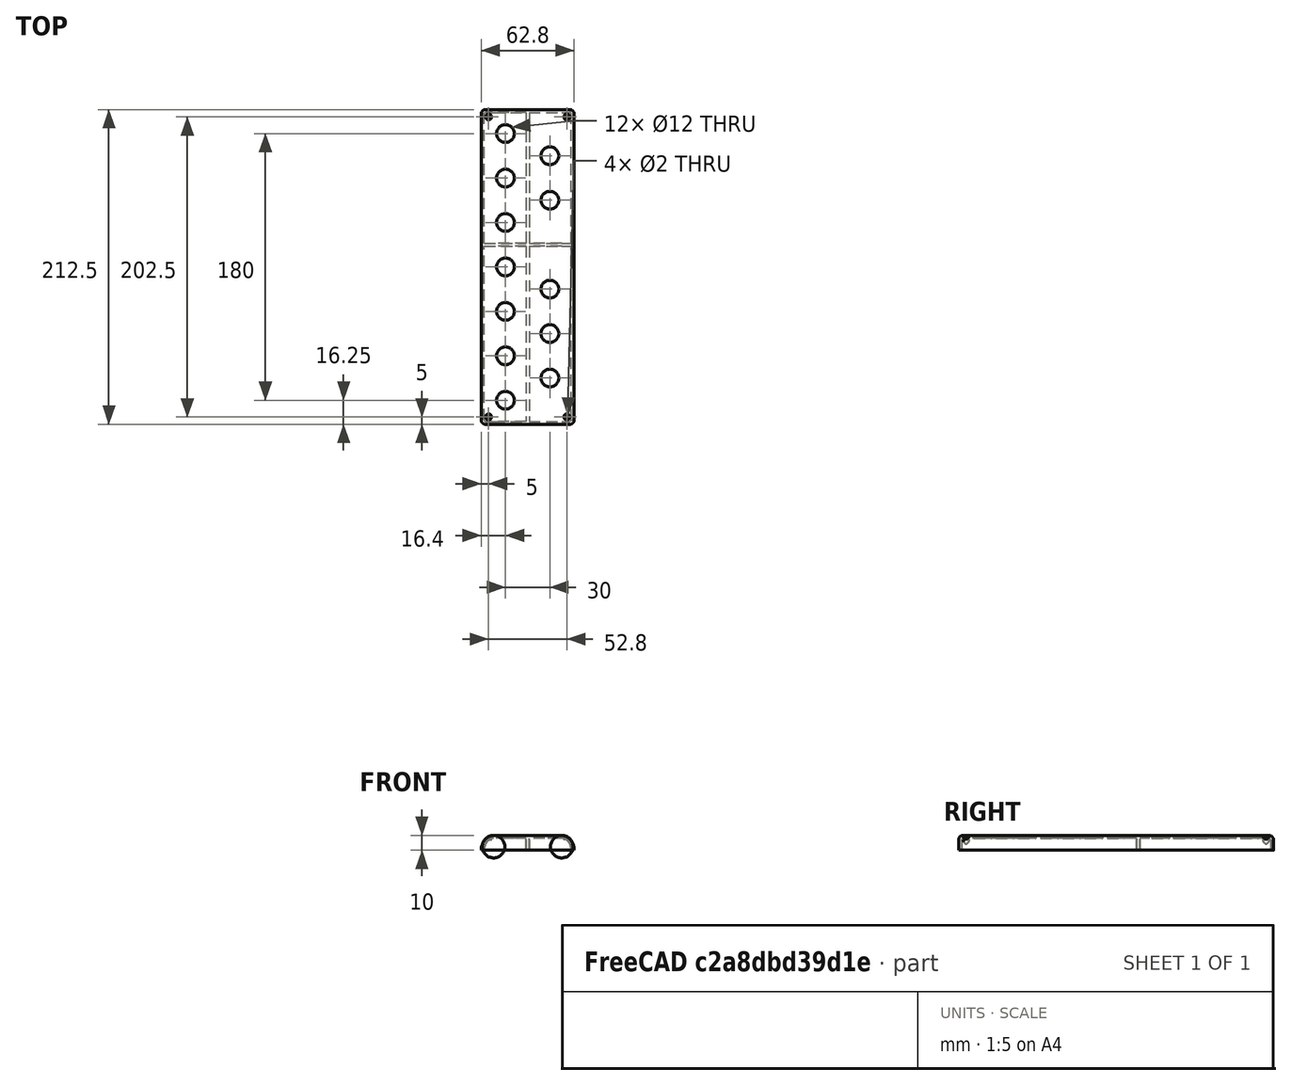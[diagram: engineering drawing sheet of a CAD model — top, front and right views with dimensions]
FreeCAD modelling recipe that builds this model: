
FCSTD DOCUMENT  (FreeCAD 0.20R28671 (Git))
Label: cubierta
License: All rights reserved
LicenseURL: http://en.wikipedia.org/wiki/All_rights_reserved
objects: TechDraw::DrawViewDimension×25, Sketcher::SketchObject×8, TechDraw::DrawViewAnnotation×5, PartDesign::Pad×4, PartDesign::Pocket×2, PartDesign::Plane×2, TechDraw::DrawProjGroupItem×2, TechDraw::DrawViewSection×2, PartDesign::Fillet×1, PartDesign::Thickness×1, PartDesign::Body×1, TechDraw::DrawSVGTemplate×1, TechDraw::DrawProjGroup×1, TechDraw::DrawPage×1
note: 27 computed .brp shape members not serialized (recipe doc carries the construction recipe); baked Part::Feature solids carry a one-line shape summary decoded from their .brp

FEATURE [Sketcher::SketchObject] Sketch
  FullyConstrained = true
  MapMode = 5
  Placement = pos=(0,0,0) rot=(1,0,0;1.5708rad)
  Support = -> [XZ_Plane]
  sketch-geometry (12):
    g0: LineSegment StartX=0 StartY=1.2153e-11 StartZ=0 EndX=-31.4 EndY=5.028e-13 EndZ=0
    g1: LineSegment StartX=0 StartY=1.2153e-11 StartZ=0 EndX=31.4 EndY=1.2153e-11 EndZ=0
    g2: LineSegment StartX=-23 StartY=10 StartZ=0 EndX=0 EndY=10 EndZ=0
    g3: LineSegment StartX=0 StartY=10 StartZ=0 EndX=23 EndY=10 EndZ=0
    g4: LineSegment StartX=-31.4 StartY=5.028e-13 StartZ=0 EndX=-28 EndY=0 EndZ=0
    g5: LineSegment StartX=-28 StartY=0 StartZ=0 EndX=-28 EndY=7 EndZ=0
    g6: ArcOfCircle CenterX=-23 CenterY=2.41173 CenterZ=0 NormalX=0 NormalY=0 NormalZ=1 AngleXU=0 Radius=7.58827 StartAngle=1.5708 EndAngle=2.49226
    g7: ArcOfCircle CenterX=-19.8231 CenterY=-1.6781e-06 CenterZ=0 NormalX=0 NormalY=0 NormalZ=1 AngleXU=0 Radius=11.5769 StartAngle=2.49226 EndAngle=3.14159
    g8: LineSegment StartX=-31.4 StartY=5.028e-13 StartZ=0 EndX=-31.4 EndY=7 EndZ=0
    g9: ArcOfCircle CenterX=23 CenterY=2.41173 CenterZ=0 NormalX=0 NormalY=0 NormalZ=1 AngleXU=0 Radius=7.58827 StartAngle=0.649332 EndAngle=1.5708
    g10: ArcOfCircle CenterX=19.8231 CenterY=7.13302e-06 CenterZ=0 NormalX=0 NormalY=0 NormalZ=1 AngleXU=0 Radius=11.5769 StartAngle=6.28318 EndAngle=6.93252
    g11: LineSegment StartX=31.4 StartY=1.2153e-11 StartZ=0 EndX=31.4 EndY=10 EndZ=0
  constraints (35):
    c: Coincident(g0,g-1)
    c: PointOnObject(g0,g-1)
    c: Coincident(g1,g0)
    c: Horizontal(g1)
    c: Equal(g1,g0)
    c: DistanceX(g0,g1) = 62.8
    c: Coincident(g3,g2)
    c: Horizontal(g3)
    c: Vertical(g0,g2)
    c: Equal(g2,g3)
    c: DistanceX(g2,g3) = 46
    c: DistanceY(g0,g2) = 10
    c: Horizontal(g2)
    c: Coincident(g4,g0)
    c: PointOnObject(g4,g0)
    c: Coincident(g5,g4)
    c: Vertical(g5)
    c: DistanceX(g0,g4) = 3.4
    c: DistanceY(g5,g5) = 7
    c: Tangent(g6,g2) = 1.5708
    c: Coincident(g7,g0)
    c: Horizontal(g6,g5)
    c: Tangent(g7,g6) = -1.5708
    c: Coincident(g8,g0)
    c: Vertical(g8)
    c: Tangent(g7,g8)
    c: Horizontal(g8,g5)
    c: Coincident(g10,g1)
    c: Tangent(g9,g3) = 1.5708
    c: Coincident(g11,g1)
    c: Vertical(g11)
    c: Horizontal(g11,g3)
    c: Tangent(g10,g11)
    c: Equal(g9,g6)
    c: Tangent(g9,g10) = -1.5708
FEATURE [PartDesign::Pad] Pad
  Direction = (0,-1,-2e-16)
  Length = 212.5
  Length2 = 100
  Placement = pos=(0,0,0) rot=(1,0,0;1.5708rad)
  Profile = -> Sketch
  ReferenceAxis = -> Sketch [N_Axis]
  Type = 0
FEATURE [PartDesign::Fillet] Fillet
  Base = -> Pad [Edge19,Edge18]
  BaseFeature = -> Pad
  Placement = pos=(0,0,0) rot=(1,0,0;1.5708rad)
  Radius = 3
  SupportTransform = false
  UseAllEdges = false
FEATURE [PartDesign::Thickness] Thickness
  Base = -> Fillet [Face7,Face1]
  BaseFeature = -> Fillet
  Intersection = false
  Join = 0
  Mode = 0
  Reversed = true
  SupportTransform = false
  Value = 2
FEATURE [Sketcher::SketchObject] Sketch001
  ExternalGeometry = -> [Thickness]
  FullyConstrained = true
  MapMode = 5
  Placement = pos=(0,0,1.2153e-11) rot=(1,0,0;3.14159rad)
  Support = -> [Thickness]
  sketch-geometry (12):
    g0: LineSegment StartX=-31.4 StartY=207.5 StartZ=0 EndX=-26.4 EndY=207.5 EndZ=0
    g1: LineSegment StartX=-26.4 StartY=207.5 StartZ=0 EndX=-26.4 EndY=212.5 EndZ=0
    g2: LineSegment StartX=26.4 StartY=212.5 StartZ=0 EndX=26.4 EndY=207.5 EndZ=0
    g3: LineSegment StartX=26.4 StartY=207.5 StartZ=0 EndX=31.4 EndY=207.5 EndZ=0
    g4: LineSegment StartX=-31.4 StartY=5 StartZ=0 EndX=-26.4 EndY=5 EndZ=0
    g5: LineSegment StartX=-26.4 StartY=5 StartZ=0 EndX=-26.4 EndY=0 EndZ=0
    g6: LineSegment StartX=26.4 StartY=0 StartZ=0 EndX=26.4 EndY=5 EndZ=0
    g7: LineSegment StartX=26.4 StartY=5 StartZ=0 EndX=31.4 EndY=5 EndZ=0
    g8: Circle CenterX=-26.4 CenterY=207.5 CenterZ=0 NormalX=0 NormalY=0 NormalZ=1 AngleXU=0 Radius=2
    g9: Circle CenterX=26.4 CenterY=207.5 CenterZ=0 NormalX=0 NormalY=0 NormalZ=1 AngleXU=0 Radius=2
    g10: Circle CenterX=-26.4 CenterY=5 CenterZ=0 NormalX=0 NormalY=0 NormalZ=1 AngleXU=0 Radius=2
    g11: Circle CenterX=26.4 CenterY=5 CenterZ=0 NormalX=0 NormalY=0 NormalZ=1 AngleXU=0 Radius=2
  constraints (36):
    c: PointOnObject(g1,g-7)
    c: PointOnObject(g0,g-5)
    c: PointOnObject(g2,g-8)
    c: PointOnObject(g3,g-6)
    c: PointOnObject(g7,g-6)
    c: PointOnObject(g6,g-4)
    c: PointOnObject(g5,g-3)
    c: PointOnObject(g4,g-5)
    c: Vertical(g5)
    c: Horizontal(g4)
    c: Vertical(g6)
    c: Horizontal(g7)
    c: Vertical(g1)
    c: Horizontal(g0)
    c: Horizontal(g3)
    c: Vertical(g2)
    c: Coincident(g9,g2)
    c: Coincident(g9,g3)
    c: Coincident(g1,g8)
    c: Coincident(g0,g8)
    c: Coincident(g10,g4)
    c: Coincident(g10,g5)
    c: Coincident(g11,g6)
    c: Coincident(g11,g7)
    c: Equal(g7,g6)
    c: Equal(g6,g5)
    c: Equal(g5,g4)
    c: Equal(g4,g3)
    c: Equal(g3,g2)
    c: Equal(g2,g1)
    c: Equal(g1,g0)
    c: DistanceY(g1,g1) = 5
    c: Equal(g8,g9)
    c: Equal(g9,g11)
    c: Equal(g11,g10)
    c: Diameter(g10) = 4
FEATURE [PartDesign::Pocket] Pocket
  BaseFeature = -> Thickness
  Direction = (0,0,1)
  Length = 5
  Length2 = 100
  Profile = -> Sketch001
  Type = 1
FEATURE [PartDesign::Plane] DatumPlane
  AttachmentOffset = pos=(0,0,-7) rot=(0,0,1;0rad)
  Length = 119.841
  MapMode = 5
  Placement = pos=(-2.5971e-12,0,7) rot=(1,0,0;3.14159rad)
  ResizeMode = 0
  Support = -> [Pocket]
  Width = 282.746
FEATURE [Sketcher::SketchObject] Sketch002
  ExternalGeometry = -> [Pocket]
  FullyConstrained = true
  MapMode = 5
  Placement = pos=(-2.5971e-12,0,7) rot=(1,0,0;3.14159rad)
  Support = -> [DatumPlane]
  sketch-geometry (8):
    g0: Circle CenterX=26.4 CenterY=5 CenterZ=0 NormalX=0 NormalY=0 NormalZ=1 AngleXU=0 Radius=2
    g1: Circle CenterX=-26.4 CenterY=5 CenterZ=0 NormalX=0 NormalY=0 NormalZ=1 AngleXU=0 Radius=2
    g2: Circle CenterX=-26.4 CenterY=207.5 CenterZ=0 NormalX=0 NormalY=0 NormalZ=1 AngleXU=0 Radius=2
    g3: Circle CenterX=26.4 CenterY=207.5 CenterZ=0 NormalX=0 NormalY=0 NormalZ=1 AngleXU=0 Radius=2
    g4: Circle CenterX=-26.4 CenterY=207.5 CenterZ=0 NormalX=0 NormalY=0 NormalZ=1 AngleXU=0 Radius=1
    g5: Circle CenterX=26.4 CenterY=207.5 CenterZ=0 NormalX=0 NormalY=0 NormalZ=1 AngleXU=0 Radius=1
    g6: Circle CenterX=26.4 CenterY=5 CenterZ=0 NormalX=0 NormalY=0 NormalZ=1 AngleXU=0 Radius=1
    g7: Circle CenterX=-26.4 CenterY=5 CenterZ=0 NormalX=0 NormalY=0 NormalZ=1 AngleXU=0 Radius=1
  constraints (20):
    c: PointOnObject(g-10,g0)
    c: PointOnObject(g-10,g0)
    c: PointOnObject(g-9,g0)
    c: PointOnObject(g-7,g1)
    c: PointOnObject(g-8,g1)
    c: PointOnObject(g-8,g1)
    c: PointOnObject(g-4,g2)
    c: PointOnObject(g-4,g2)
    c: PointOnObject(g-3,g2)
    c: PointOnObject(g-5,g3)
    c: PointOnObject(g-6,g3)
    c: PointOnObject(g-5,g3)
    c: Coincident(g4,g2)
    c: Coincident(g5,g3)
    c: Coincident(g6,g0)
    c: Coincident(g7,g1)
    c: Equal(g7,g6)
    c: Equal(g6,g5)
    c: Equal(g5,g4)
    c: Diameter(g4) = 2
FEATURE [PartDesign::Pad] Pad001
  BaseFeature = -> Pocket
  Direction = (3.71e-13,0,-1)
  Length = 0.9
  Length2 = 100
  Profile = -> Sketch002
  ReferenceAxis = -> Sketch002 [N_Axis]
  Reversed = true
  Type = 0
FEATURE [Sketcher::SketchObject] Sketch003
  ExternalGeometry = -> [Pad001]
  FullyConstrained = true
  MapMode = 5
  Placement = pos=(-2.5971e-12,0,7) rot=(1,0,0;3.14159rad)
  Support = -> [Pad001]
  sketch-geometry (33):
    g0: Circle CenterX=-15 CenterY=16.25 CenterZ=0 NormalX=0 NormalY=0 NormalZ=1 AngleXU=0 Radius=6
    g1: Circle CenterX=-15 CenterY=46.25 CenterZ=0 NormalX=0 NormalY=0 NormalZ=1 AngleXU=0 Radius=6
    g2: Circle CenterX=-15 CenterY=76.25 CenterZ=0 NormalX=0 NormalY=0 NormalZ=1 AngleXU=0 Radius=6
    g3: Circle CenterX=-15 CenterY=106.25 CenterZ=0 NormalX=0 NormalY=0 NormalZ=1 AngleXU=0 Radius=6
    g4: Circle CenterX=-15 CenterY=136.25 CenterZ=0 NormalX=0 NormalY=0 NormalZ=1 AngleXU=0 Radius=6
    g5: LineSegment StartX=-15 StartY=46.25 StartZ=0 EndX=-15 EndY=16.25 EndZ=0
    g6: LineSegment StartX=-15 StartY=16.25 StartZ=0 EndX=-15 EndY=46.25 EndZ=0
    g7: LineSegment StartX=-15 StartY=46.25 StartZ=0 EndX=-15 EndY=76.25 EndZ=0
    g8: LineSegment StartX=-15 StartY=76.25 StartZ=0 EndX=-15 EndY=106.25 EndZ=0
    g9: LineSegment StartX=-15 StartY=106.25 StartZ=0 EndX=-15 EndY=136.25 EndZ=0
    g10: LineSegment StartX=-15 StartY=136.25 StartZ=0 EndX=-15 EndY=106.25 EndZ=0
    g11: Circle CenterX=15 CenterY=31.25 CenterZ=0 NormalX=0 NormalY=0 NormalZ=1 AngleXU=0 Radius=6
    g12: Circle CenterX=15 CenterY=61.25 CenterZ=0 NormalX=0 NormalY=0 NormalZ=1 AngleXU=0 Radius=6
    g13: Circle CenterX=15 CenterY=121.25 CenterZ=0 NormalX=0 NormalY=0 NormalZ=1 AngleXU=0 Radius=6
    g14: Circle CenterX=15 CenterY=151.25 CenterZ=0 NormalX=0 NormalY=0 NormalZ=1 AngleXU=0 Radius=6
    g15: LineSegment StartX=15 StartY=31.25 StartZ=0 EndX=15 EndY=61.25 EndZ=0
    g16: LineSegment StartX=15 StartY=91.25 StartZ=0 EndX=15 EndY=121.25 EndZ=0
    g17: LineSegment StartX=15 StartY=121.25 StartZ=0 EndX=15 EndY=151.25 EndZ=0
    g18: LineSegment StartX=15 StartY=31.25 StartZ=0 EndX=-15 EndY=46.25 EndZ=0
    g19: LineSegment StartX=15 StartY=31.25 StartZ=0 EndX=-15 EndY=16.25 EndZ=0
    g20: LineSegment StartX=15 StartY=91.25 StartZ=0 EndX=-15 EndY=76.25 EndZ=0
    g21: LineSegment StartX=15 StartY=91.25 StartZ=0 EndX=-15 EndY=106.25 EndZ=0
    g22: LineSegment StartX=15 StartY=31.25 StartZ=0 EndX=0 EndY=31.25 EndZ=0
    g23: LineSegment StartX=0 StartY=31.25 StartZ=0 EndX=-15 EndY=31.25 EndZ=0
    g24: LineSegment StartX=0 StartY=0 StartZ=0 EndX=0 EndY=212.5 EndZ=0
    g25: LineSegment StartX=-15 StartY=16.25 StartZ=0 EndX=-15 EndY=0 EndZ=0
    g26: Circle CenterX=15 CenterY=181.25 CenterZ=0 NormalX=0 NormalY=0 NormalZ=1 AngleXU=0 Radius=6
    g27: Circle CenterX=-15 CenterY=166.25 CenterZ=0 NormalX=0 NormalY=0 NormalZ=1 AngleXU=0 Radius=6
    g28: Circle CenterX=-15 CenterY=196.25 CenterZ=0 NormalX=0 NormalY=0 NormalZ=1 AngleXU=0 Radius=6
    g29: LineSegment StartX=15 StartY=181.25 StartZ=0 EndX=15 EndY=151.25 EndZ=0
    g30: LineSegment StartX=-15 StartY=136.25 StartZ=0 EndX=-15 EndY=166.25 EndZ=0
    g31: LineSegment StartX=-15 StartY=166.25 StartZ=0 EndX=-15 EndY=196.25 EndZ=0
    g32: LineSegment StartX=-15 StartY=196.25 StartZ=0 EndX=-15 EndY=212.5 EndZ=0
  constraints (85):
    c: Equal(g0,g1)
    c: Equal(g1,g2)
    c: Equal(g2,g3)
    c: Equal(g3,g4)
    c: Coincident(g5,g0)
    c: Vertical(g5)
    c: Coincident(g6,g0)
    c: Coincident(g6,g1)
    c: Vertical(g6)
    c: Coincident(g7,g1)
    c: Coincident(g7,g2)
    c: Coincident(g8,g2)
    c: Coincident(g8,g3)
    c: Coincident(g9,g3)
    c: Coincident(g9,g4)
    c: Coincident(g10,g4)
    c: Equal(g8,g7)
    c: Equal(g7,g6)
    c: Equal(g6,g5)
    c: Equal(g5,g9)
    c: Equal(g9,g10)
    c: Vertical(g8)
    c: Vertical(g7)
    c: Vertical(g9)
    c: Vertical(g10)
    c: Equal(g14,g13)
    c: Equal(g12,g11)
    c: Equal(g11,g0)
    c: Coincident(g15,g11)
    c: Coincident(g15,g12)
    c: Vertical(g15)
    c: Coincident(g16,g13)
    c: Coincident(g17,g13)
    c: Coincident(g17,g14)
    c: Vertical(g17)
    c: Vertical(g16)
    c: Equal(g17,g16)
    c: Equal(g16,g15)
    c: Equal(g15,g6)
    c: Coincident(g18,g11)
    c: Coincident(g19,g11)
    c: Coincident(g19,g0)
    c: Equal(g19,g18)
    c: Coincident(g20,g2)
    c: Coincident(g21,g3)
    c: Equal(g21,g20)
    c: Coincident(g22,g11)
    c: Horizontal(g22)
    c: Coincident(g23,g22)
    c: PointOnObject(g23,g5)
    c: Horizontal(g23)
    c: Equal(g23,g22)
    c: Coincident(g24,g-1)
    c: Coincident(g24,g-3)
    c: PointOnObject(g22,g24)
    c: Coincident(g25,g0)
    c: PointOnObject(g25,g-1)
    c: Vertical(g25)
    c: Equal(g26,g27)
    c: Equal(g27,g28)
    c: Equal(g28,g4)
    c: Coincident(g29,g26)
    c: Coincident(g29,g14)
    c: Coincident(g30,g4)
    c: Coincident(g30,g27)
    c: Coincident(g31,g27)
    c: Coincident(g31,g28)
    c: Vertical(g31)
    c: Vertical(g30)
    c: Vertical(g29)
    c: Equal(g31,g30)
    c: Equal(g30,g29)
    c: Equal(g29,g17)
    c: Coincident(g20,g16)
    c: Coincident(g16,g21)
    c: Coincident(g32,g28)
    c: Horizontal(g32,g24)
    c: Vertical(g32)
    c: Equal(g25,g32)
    c: Vertical(g16,g12)
    c: Equal(g14,g26)
    c: Diameter(g0) = 12
    c: DistanceX(g23,g11) = 30
    c: DistanceY(g0,g1) = 30
    c: Coincident(g18,g1)
FEATURE [PartDesign::Pocket] Pocket001
  BaseFeature = -> Pad001
  Direction = (-3.71e-13,0,1)
  Length = 5
  Length2 = 100
  Profile = -> Sketch003
  Type = 1
FEATURE [Sketcher::SketchObject] Sketch004
  ExternalGeometry = -> [Pocket001]
  FullyConstrained = true
  MapMode = 5
  Placement = pos=(0,0,1.2153e-11) rot=(1,0,0;3.14159rad)
  Support = -> [Pocket001]
  sketch-geometry (9):
    g0: LineSegment StartX=0 StartY=1 StartZ=0 EndX=-1 EndY=1 EndZ=0
    g1: LineSegment StartX=0 StartY=1 StartZ=0 EndX=1 EndY=1 EndZ=0
    g2: LineSegment StartX=-1 StartY=1 StartZ=0 EndX=-1 EndY=211.5 EndZ=0
    g3: LineSegment StartX=1 StartY=1 StartZ=0 EndX=1 EndY=211.5 EndZ=0
    g4: LineSegment StartX=-1 StartY=211.5 StartZ=0 EndX=1 EndY=211.5 EndZ=0
    g5: LineSegment StartX=0 StartY=2 StartZ=0 EndX=0 EndY=1 EndZ=0
    g6: LineSegment StartX=0 StartY=1 StartZ=0 EndX=0 EndY=0 EndZ=0
    g7: LineSegment StartX=0 StartY=210.5 StartZ=0 EndX=0 EndY=211.5 EndZ=0
    g8: LineSegment StartX=0 StartY=211.5 StartZ=0 EndX=0 EndY=212.5 EndZ=0
  constraints (24):
    c: Coincident(g2,g0)
    c: Vertical(g2)
    c: Coincident(g3,g1)
    c: Vertical(g3)
    c: Coincident(g4,g2)
    c: Coincident(g4,g3)
    c: Horizontal(g4)
    c: Equal(g0,g1)
    c: DistanceX(g0,g1) = 2
    c: Coincident(g0,g1)
    c: Horizontal(g0)
    c: Coincident(g5,g-4)
    c: Coincident(g5,g0)
    c: Vertical(g5)
    c: Coincident(g6,g0)
    c: Coincident(g6,g-1)
    c: Equal(g6,g5)
    c: Horizontal(g1)
    c: Coincident(g7,g-5)
    c: PointOnObject(g7,g4)
    c: Coincident(g8,g7)
    c: Coincident(g8,g-3)
    c: Vertical(g8)
    c: Equal(g8,g7)
FEATURE [PartDesign::Pad] Pad002
  BaseFeature = -> Pocket001
  Direction = (3.71e-13,0,-1)
  Length = 10
  Length2 = 100
  Profile = -> Sketch004
  ReferenceAxis = -> Sketch004 [N_Axis]
  Type = 3
  UpToFace = -> Pocket001 [Face64]
FEATURE [Sketcher::SketchObject] Sketch005
  ExternalGeometry = -> [Pad002]
  FullyConstrained = true
  MapMode = 5
  Placement = pos=(0,0,1.2153e-11) rot=(1,0,0;3.14159rad)
  Support = -> [Pad002]
  sketch-geometry (6):
    g0: LineSegment StartX=-31.4 StartY=92.25 StartZ=0 EndX=31.4 EndY=92.25 EndZ=0
    g1: LineSegment StartX=31.4 StartY=92.25 StartZ=0 EndX=31.4 EndY=90.25 EndZ=0
    g2: LineSegment StartX=31.4 StartY=90.25 StartZ=0 EndX=-31.4 EndY=90.25 EndZ=0
    g3: LineSegment StartX=-31.4 StartY=90.25 StartZ=0 EndX=-31.4 EndY=92.25 EndZ=0
    g4: LineSegment StartX=-15 StartY=76.25 StartZ=0 EndX=-15 EndY=90.25 EndZ=0
    g5: LineSegment StartX=-15 StartY=106.25 StartZ=0 EndX=-15 EndY=92.25 EndZ=0
  constraints (18):
    c: Coincident(g0,g1)
    c: Coincident(g1,g2)
    c: Coincident(g2,g3)
    c: Coincident(g3,g0)
    c: Horizontal(g0)
    c: Horizontal(g2)
    c: Vertical(g1)
    c: Vertical(g3)
    c: DistanceY(g2,g0) = 2
    c: Coincident(g4,g-6)
    c: PointOnObject(g4,g2)
    c: Vertical(g4)
    c: Coincident(g5,g-5)
    c: PointOnObject(g5,g0)
    c: Vertical(g5)
    c: Equal(g5,g4)
    c: PointOnObject(g0,g-7)
    c: PointOnObject(g0,g-8)
FEATURE [PartDesign::Plane] DatumPlane001
  Length = 63.3962
  MapMode = 1
  Placement = pos=(31.4,-92.25,1.2153e-11) rot=(0.57735,-0.57735,0.57735;2.0944rad)
  ResizeMode = 0
  Support = -> [Sketch005]
  Width = 103.125
FEATURE [Sketcher::SketchObject] Sketch006
  ExternalGeometry = -> [Sketch]
  FullyConstrained = true
  MapMode = 5
  Placement = pos=(31.4,-92.25,1.2153e-11) rot=(0.57735,-0.57735,0.57735;2.0944rad)
  Support = -> [DatumPlane001]
  sketch-geometry (6):
    g0: LineSegment StartX=-1.16297e-11 StartY=62.8 StartZ=0 EndX=1.216e-12 EndY=6.5654e-12 EndZ=0
    g1: LineSegment StartX=10 StartY=54.4 StartZ=0 EndX=10 EndY=8.4 EndZ=0
    g2: ArcOfCircle CenterX=-1.67812e-06 CenterY=51.2231 CenterZ=0 NormalX=0 NormalY=0 NormalZ=1 AngleXU=0 Radius=11.5769 StartAngle=0.921466 EndAngle=1.5708
    g3: ArcOfCircle CenterX=2.41173 CenterY=54.4 CenterZ=0 NormalX=0 NormalY=0 NormalZ=1 AngleXU=0 Radius=7.58827 StartAngle=-6.235e-13 EndAngle=0.921466
    g4: ArcOfCircle CenterX=2.41173 CenterY=8.4 CenterZ=0 NormalX=0 NormalY=0 NormalZ=1 AngleXU=0 Radius=7.58827 StartAngle=5.36172 EndAngle=6.28319
    g5: ArcOfCircle CenterX=7.13304e-06 CenterY=11.5769 CenterZ=0 NormalX=0 NormalY=0 NormalZ=1 AngleXU=0 Radius=11.5769 StartAngle=4.71239 EndAngle=5.36172
  constraints (16):
    c: Coincident(g0,g-5)
    c: Coincident(g0,g-1)
    c: Coincident(g1,g-4)
    c: Coincident(g1,g-7)
    c: Coincident(g2,g0)
    c: Coincident(g2,g-5)
    c: Tangent(g2,g-5)
    c: Coincident(g3,g2)
    c: Coincident(g3,g1)
    c: Tangent(g3,g-4)
    c: Coincident(g4,g1)
    c: Coincident(g4,g-8)
    c: Tangent(g4,g-7)
    c: Coincident(g5,g4)
    c: Coincident(g5,g0)
    c: Tangent(g5,g-8)
FEATURE [PartDesign::Pad] Pad003
  BaseFeature = -> Pad002
  Direction = (0,-1,0)
  Length = 2
  Length2 = 100
  Profile = -> Sketch006
  ReferenceAxis = -> Sketch006 [N_Axis]
  Reversed = true
  Type = 0
FEATURE [Sketcher::SketchObject] Sketch007
  ExternalGeometry = -> [Pad003]
  FullyConstrained = false
  MapMode = 5
  Placement = pos=(0,0,1.2153e-11) rot=(1,0,0;3.14159rad)
  Support = -> [Pad003]
  sketch-geometry (6):
    g0: LineSegment StartX=-31.4 StartY=92.25 StartZ=0 EndX=-31.4 EndY=91.25 EndZ=0
    g1: LineSegment StartX=-31.4 StartY=91.25 StartZ=0 EndX=-31.4 EndY=90.25 EndZ=0
    g2: LineSegment StartX=-37.6108 StartY=91.25 StartZ=0 EndX=52.1178 EndY=91.25 EndZ=0
    g3: LineSegment StartX=52.1178 StartY=91.25 StartZ=0 EndX=52.1178 EndY=227.634 EndZ=0
    g4: LineSegment StartX=52.1178 StartY=227.634 StartZ=0 EndX=-37.6108 EndY=227.634 EndZ=0
    g5: LineSegment StartX=-37.6108 StartY=227.634 StartZ=0 EndX=-37.6108 EndY=91.25 EndZ=0
  constraints (14):
    c: Coincident(g0,g-3)
    c: Vertical(g0)
    c: Coincident(g1,g0)
    c: Coincident(g1,g-4)
    c: Equal(g0,g1)
    c: Coincident(g2,g3)
    c: Coincident(g3,g4)
    c: Coincident(g4,g5)
    c: Coincident(g5,g2)
    c: Horizontal(g2)
    c: Horizontal(g4)
    c: Vertical(g3)
    c: Vertical(g5)
    c: PointOnObject(g0,g2)
FEATURE [PartDesign::Body] Body
  Group = -> [Sketch,Pad,Fillet,Thickness,Sketch001,Pocket,DatumPlane,Sketch002,Pad001,Sketch003,Pocket001,Sketch004,Pad002,Sketch005,DatumPlane001,Sketch006,Pad003,Sketch007]
  Origin = -> Origin
  Tip = -> Pad003
FEATURE [TechDraw::DrawSVGTemplate] Template
  EditableTexts = AUTHOR_NAME=Daniel García García; DATE=15-04-2022; DN=15; DOCUMENT_TYPE=Plano de pieza; PN=23; REVISION=1; SCALE=1:1; SHEET=15/15; SIZE=A4; TITLELINE-1=Cubierta Superior
  Height = 210
  Orientation = 1
  Width = 297
FEATURE [TechDraw::DrawProjGroupItem] ProjItem  label="Front"
  CoarseView = false
  Direction = (-1,0,0)
  Focus = 100
  HardHidden = false
  IsoCount = 0
  IsoHidden = false
  IsoVisible = false
  LockPosition = true
  Perspective = false
  Rotation = 0
  RotationVector = (0,-1,0)
  ScaleType = 2
  SeamHidden = false
  SeamVisible = true
  SmoothHidden = false
  SmoothVisible = true
  Source = -> [Pad003]
  Type = 0
  X = 0
  XDirection = (0,-1,0)
  Y = 0
FEATURE [TechDraw::DrawProjGroupItem] ProjItem001  label="Top"
  CoarseView = false
  Direction = (0,0,1)
  Focus = 100
  HardHidden = false
  IsoCount = 0
  IsoHidden = false
  IsoVisible = false
  LockPosition = true
  Perspective = false
  Rotation = 0
  RotationVector = (1,0,0)
  ScaleType = 2
  SeamHidden = false
  SeamVisible = true
  SmoothHidden = false
  SmoothVisible = true
  Source = -> [Pad003]
  Type = 4
  X = 0
  XDirection = (0,-1,0)
  Y = -90.7058
FEATURE [TechDraw::DrawProjGroup] ProjGroup
  Anchor = -> ProjItem
  AutoDistribute = true
  LockPosition = true
  ProjectionType = 0
  Rotation = 0
  ScaleType = 0
  Source = -> [Pad003]
  Views = -> [ProjItem,ProjItem001]
  X = 152.056
  Y = 178.296
  spacingX = 15
  spacingY = 15
FEATURE [TechDraw::DrawViewDimension] Dimension
  AngleOverride = false
  Arbitrary = false
  ArbitraryTolerances = false
  EqualTolerance = true
  ExtensionAngle = 0
  FormatSpec = %.2w
  FormatSpecOverTolerance = %+.2w
  FormatSpecUnderTolerance = %+.2w
  Inverted = false
  LineAngle = 0
  LockPosition = false
  MeasureType = 1
  OverTolerance = 0
  References2D = -> [ProjItem]
  Rotation = 0
  ScaleType = 0
  TheoreticalExact = false
  Type = 1
  UnderTolerance = 0
  X = 2.1598
  Y = 15.6269
FEATURE [TechDraw::DrawViewDimension] Dimension001
  AngleOverride = false
  Arbitrary = false
  ArbitraryTolerances = false
  EqualTolerance = true
  ExtensionAngle = 0
  FormatSpec = ⌀%.2w
  FormatSpecOverTolerance = %+.2w
  FormatSpecUnderTolerance = %+.2w
  Inverted = false
  LineAngle = 0
  LockPosition = false
  MeasureType = 1
  OverTolerance = 0
  References2D = -> [ProjItem001]
  Rotation = 0
  ScaleType = 0
  TheoreticalExact = false
  Type = 5
  UnderTolerance = 0
  X = -93.626
  Y = 7.7505
FEATURE [TechDraw::DrawViewDimension] Dimension002
  AngleOverride = false
  Arbitrary = false
  ArbitraryTolerances = false
  EqualTolerance = true
  ExtensionAngle = 0
  FormatSpec = %.2w
  FormatSpecOverTolerance = %+.2w
  FormatSpecUnderTolerance = %+.2w
  Inverted = false
  LineAngle = 0
  LockPosition = false
  MeasureType = 1
  OverTolerance = 0
  References2D = -> [ProjItem]
  Rotation = 0
  ScaleType = 0
  TheoreticalExact = false
  Type = 1
  UnderTolerance = 0
  X = 0.67922
  Y = -5.55649
FEATURE [TechDraw::DrawViewDimension] Dimension003
  AngleOverride = false
  Arbitrary = false
  ArbitraryTolerances = false
  EqualTolerance = true
  ExtensionAngle = 0
  FormatSpec = %.2w
  FormatSpecOverTolerance = %+.2w
  FormatSpecUnderTolerance = %+.2w
  Inverted = false
  LineAngle = 0
  LockPosition = false
  MeasureType = 1
  OverTolerance = 0
  References2D = -> [ProjItem]
  Rotation = 0
  ScaleType = 0
  TheoreticalExact = false
  Type = 2
  UnderTolerance = 0
  X = -115.985
  Y = 2.73584
FEATURE [TechDraw::DrawViewDimension] Dimension004
  AngleOverride = false
  Arbitrary = false
  ArbitraryTolerances = false
  EqualTolerance = true
  ExtensionAngle = 0
  FormatSpec = R%.2w
  FormatSpecOverTolerance = %+.2w
  FormatSpecUnderTolerance = %+.2w
  Inverted = false
  LineAngle = 0
  LockPosition = false
  MeasureType = 1
  OverTolerance = 0
  References2D = -> [ProjItem]
  Rotation = 0
  ScaleType = 0
  TheoreticalExact = false
  Type = 4
  UnderTolerance = 0
  X = -116.741
  Y = 16.5088
FEATURE [TechDraw::DrawViewDimension] Dimension005
  AngleOverride = false
  Arbitrary = false
  ArbitraryTolerances = false
  EqualTolerance = true
  ExtensionAngle = 0
  FormatSpec = %.2w
  FormatSpecOverTolerance = %+.2w
  FormatSpecUnderTolerance = %+.2w
  Inverted = false
  LineAngle = 0
  LockPosition = false
  MeasureType = 1
  OverTolerance = 0
  References2D = -> [ProjItem001]
  Rotation = 0
  ScaleType = 0
  TheoreticalExact = false
  Type = 2
  UnderTolerance = 0
  X = -129.814
  Y = 2.22098
FEATURE [TechDraw::DrawViewDimension] Dimension006
  AngleOverride = false
  Arbitrary = false
  ArbitraryTolerances = false
  EqualTolerance = true
  ExtensionAngle = 0
  FormatSpec = %.2w
  FormatSpecOverTolerance = %+.2w
  FormatSpecUnderTolerance = %+.2w
  Inverted = false
  LineAngle = 0
  LockPosition = false
  MeasureType = 1
  OverTolerance = 0
  References2D = -> [ProjItem001]
  Rotation = 0
  ScaleType = 0
  TheoreticalExact = false
  Type = 1
  UnderTolerance = 0
  X = -73.4499
  Y = -33.6796
FEATURE [TechDraw::DrawViewDimension] Dimension007
  AngleOverride = false
  Arbitrary = false
  ArbitraryTolerances = false
  EqualTolerance = true
  ExtensionAngle = 0
  FormatSpec = %.2w
  FormatSpecOverTolerance = %+.2w
  FormatSpecUnderTolerance = %+.2w
  Inverted = false
  LineAngle = 0
  LockPosition = false
  MeasureType = 1
  OverTolerance = 0
  References2D = -> [ProjItem001]
  Rotation = 0
  ScaleType = 0
  TheoreticalExact = false
  Type = 1
  UnderTolerance = 0
  X = -97.9342
  Y = -34.1512
FEATURE [TechDraw::DrawViewDimension] Dimension008
  AngleOverride = false
  Arbitrary = false
  ArbitraryTolerances = false
  EqualTolerance = true
  ExtensionAngle = 0
  FormatSpec = %.2w
  FormatSpecOverTolerance = %+.2w
  FormatSpecUnderTolerance = %+.2w
  Inverted = false
  LineAngle = 0
  LockPosition = false
  MeasureType = 1
  OverTolerance = 0
  References2D = -> [ProjItem001]
  Rotation = 0
  ScaleType = 0
  TheoreticalExact = false
  Type = 2
  UnderTolerance = 0
  X = -23.3496
  Y = 0.849119
FEATURE [TechDraw::DrawViewDimension] Dimension009
  AngleOverride = false
  Arbitrary = false
  ArbitraryTolerances = false
  EqualTolerance = true
  ExtensionAngle = 0
  FormatSpec = %.2w
  FormatSpecOverTolerance = %+.2w
  FormatSpecUnderTolerance = %+.2w
  Inverted = false
  LineAngle = 0
  LockPosition = false
  MeasureType = 1
  OverTolerance = 0
  References2D = -> [ProjItem001]
  Rotation = 0
  ScaleType = 0
  TheoreticalExact = false
  Type = 2
  UnderTolerance = 0
  X = -23.5451
  Y = 24.8811
FEATURE [TechDraw::DrawViewDimension] Dimension010
  AngleOverride = false
  Arbitrary = false
  ArbitraryTolerances = false
  EqualTolerance = true
  ExtensionAngle = 0
  FormatSpec = %.2w
  FormatSpecOverTolerance = %+.2w
  FormatSpecUnderTolerance = %+.2w
  Inverted = false
  LineAngle = 0
  LockPosition = false
  MeasureType = 1
  OverTolerance = 0
  References2D = -> [ProjItem001]
  Rotation = 0
  ScaleType = 0
  TheoreticalExact = false
  Type = 1
  UnderTolerance = 0
  X = 98.435
  Y = -38.2316
FEATURE [TechDraw::DrawViewDimension] Dimension011
  AngleOverride = false
  Arbitrary = false
  ArbitraryTolerances = false
  EqualTolerance = true
  ExtensionAngle = 0
  FormatSpec = %.2w
  FormatSpecOverTolerance = %+.2w
  FormatSpecUnderTolerance = %+.2w
  Inverted = false
  LineAngle = 0
  LockPosition = false
  MeasureType = 1
  OverTolerance = 0
  References2D = -> [ProjItem001]
  Rotation = 0
  ScaleType = 0
  TheoreticalExact = false
  Type = 2
  UnderTolerance = 0
  X = -33.1002
  Y = -37.1311
FEATURE [TechDraw::DrawViewDimension] Dimension012
  AngleOverride = false
  Arbitrary = false
  ArbitraryTolerances = false
  EqualTolerance = true
  ExtensionAngle = 0
  FormatSpec = R%.2w
  FormatSpecOverTolerance = %+.2w
  FormatSpecUnderTolerance = %+.2w
  Inverted = false
  LineAngle = 0
  LockPosition = false
  MeasureType = 1
  OverTolerance = 0
  References2D = -> [ProjItem001]
  Rotation = 0
  ScaleType = 0
  TheoreticalExact = false
  Type = 4
  UnderTolerance = 0
  X = 119.978
  Y = 40.3026
FEATURE [TechDraw::DrawViewDimension] Dimension013
  AngleOverride = false
  Arbitrary = false
  ArbitraryTolerances = false
  EqualTolerance = true
  ExtensionAngle = 0
  FormatSpec = ⌀%.2w
  FormatSpecOverTolerance = %+.2w
  FormatSpecUnderTolerance = %+.2w
  Inverted = false
  LineAngle = 0
  LockPosition = false
  MeasureType = 1
  OverTolerance = 0
  References2D = -> [ProjItem001]
  Rotation = 0
  ScaleType = 0
  TheoreticalExact = false
  Type = 5
  UnderTolerance = 0
  X = 122.259
  Y = -14.6032
FEATURE [TechDraw::DrawViewDimension] Dimension014
  AngleOverride = false
  Arbitrary = false
  ArbitraryTolerances = false
  EqualTolerance = true
  ExtensionAngle = 0
  FormatSpec = ⌀%.2w
  FormatSpecOverTolerance = %+.2w
  FormatSpecUnderTolerance = %+.2w
  Inverted = false
  LineAngle = 0
  LockPosition = false
  MeasureType = 1
  OverTolerance = 0
  References2D = -> [ProjItem001]
  Rotation = 0
  ScaleType = 0
  TheoreticalExact = false
  Type = 5
  UnderTolerance = 0
  X = -89.6192
  Y = 39.5032
FEATURE [TechDraw::DrawViewDimension] Dimension015
  AngleOverride = false
  Arbitrary = false
  ArbitraryTolerances = false
  EqualTolerance = true
  ExtensionAngle = 0
  FormatSpec = %.2w
  FormatSpecOverTolerance = %+.2w
  FormatSpecUnderTolerance = %+.2w
  Inverted = false
  LineAngle = 0
  LockPosition = false
  MeasureType = 1
  OverTolerance = 0
  References2D = -> [ProjItem001]
  Rotation = 0
  ScaleType = 0
  TheoreticalExact = false
  Type = 2
  UnderTolerance = 0
  X = -118.653
  Y = 2.14118
FEATURE [TechDraw::DrawViewSection] SectionView  label="Section A - A"
  BaseView = -> ProjItem001
  CoarseView = false
  CutSurfaceDisplay = 2
  Direction = (0,-1,0)
  FileGeomPattern = <path>
  FileHatchPattern = <path>
  Focus = 100
  FuseBeforeCut = false
  HardHidden = false
  HatchScale = 1
  IsoCount = 0
  IsoHidden = false
  IsoVisible = false
  LockPosition = false
  NameGeomPattern = Diamond
  Perspective = false
  Rotation = -90
  Scale = 0.5
  ScaleType = 2
  SeamHidden = false
  SeamVisible = true
  SectionDirection = 1
  SectionNormal = (0,-1,0)
  SectionOrigin = (0,-90,5)
  SectionSymbol = A
  SmoothHidden = false
  SmoothVisible = true
  Source = -> [Pad003]
  X = 205.982
  XDirection = (0,0,-1)
  Y = 147.643
FEATURE [TechDraw::DrawViewDimension] Dimension018
  AngleOverride = false
  Arbitrary = false
  ArbitraryTolerances = false
  EqualTolerance = true
  ExtensionAngle = 0
  FormatSpec = %.2w
  FormatSpecOverTolerance = %+.2w
  FormatSpecUnderTolerance = %+.2w
  Inverted = false
  LineAngle = 0
  LockPosition = false
  MeasureType = 1
  OverTolerance = 0
  References2D = -> [SectionView]
  Rotation = 0
  ScaleType = 0
  TheoreticalExact = false
  Type = 2
  UnderTolerance = 0
  X = 4.71721
  Y = -4.62741
FEATURE [TechDraw::DrawViewAnnotation] Annotation
  Font = osifont
  LineSpace = 80
  LockPosition = true
  MaxWidth = -1
  Rotation = 0
  ScaleType = 0
  Text = '
  TextSize = 5
  TextStyle = 0
  X = 137.36
  Y = 36.6473
FEATURE [TechDraw::DrawViewAnnotation] Annotation001
  Font = osifont
  LineSpace = 80
  LockPosition = true
  MaxWidth = -1
  Rotation = 0
  ScaleType = 0
  Text = Sección A-A'
  TextSize = 5
  TextStyle = 0
  X = 245.041
  Y = 148.112
FEATURE [TechDraw::DrawViewDimension] Dimension020
  AngleOverride = false
  Arbitrary = false
  ArbitraryTolerances = false
  EqualTolerance = true
  ExtensionAngle = 0
  FormatSpec = %.2w
  FormatSpecOverTolerance = %+.2w
  FormatSpecUnderTolerance = %+.2w
  Inverted = false
  LineAngle = 0
  LockPosition = false
  MeasureType = 1
  OverTolerance = 0
  References2D = -> [SectionView]
  Rotation = 0
  ScaleType = 0
  TheoreticalExact = false
  Type = 1
  UnderTolerance = 0
  X = -11.4078
  Y = -10.169
FEATURE [TechDraw::DrawViewDimension] Dimension021
  AngleOverride = false
  Arbitrary = false
  ArbitraryTolerances = false
  EqualTolerance = true
  ExtensionAngle = 0
  FormatSpec = %.2w
  FormatSpecOverTolerance = %+.2w
  FormatSpecUnderTolerance = %+.2w
  Inverted = false
  LineAngle = 0
  LockPosition = false
  MeasureType = 1
  OverTolerance = 0
  References2D = -> [SectionView]
  Rotation = 0
  ScaleType = 0
  TheoreticalExact = false
  Type = 1
  UnderTolerance = 0
  X = 20.3662
  Y = 0.706306
FEATURE [TechDraw::DrawViewDimension] Dimension022
  AngleOverride = false
  Arbitrary = false
  ArbitraryTolerances = false
  EqualTolerance = true
  ExtensionAngle = 0
  FormatSpec = %.2w
  FormatSpecOverTolerance = %+.2w
  FormatSpecUnderTolerance = %+.2w
  Inverted = false
  LineAngle = 0
  LockPosition = false
  MeasureType = 1
  OverTolerance = 0
  References2D = -> [SectionView]
  Rotation = 0
  ScaleType = 0
  TheoreticalExact = false
  Type = 1
  UnderTolerance = 0
  X = -21.5674
  Y = -5.19125
FEATURE [TechDraw::DrawViewDimension] Dimension023
  AngleOverride = false
  Arbitrary = false
  ArbitraryTolerances = false
  EqualTolerance = true
  ExtensionAngle = 0
  FormatSpec = %.2w
  FormatSpecOverTolerance = %+.2w
  FormatSpecUnderTolerance = %+.2w
  Inverted = false
  LineAngle = 0
  LockPosition = false
  MeasureType = 1
  OverTolerance = 0
  References2D = -> [SectionView]
  Rotation = 0
  ScaleType = 0
  TheoreticalExact = false
  Type = 1
  UnderTolerance = 0
  X = -0.464357
  Y = 14.1912
FEATURE [TechDraw::DrawViewAnnotation] Annotation002
  Font = osifont
  LineSpace = 80
  LockPosition = true
  MaxWidth = -1
  Rotation = 0
  ScaleType = 0
  Text = Escala 1:2
  TextSize = 5
  TextStyle = 0
  X = 245.544
  Y = 145.551
FEATURE [TechDraw::DrawViewSection] SectionView001  label="Section B - B"
  BaseView = -> ProjItem001
  CoarseView = false
  CutSurfaceDisplay = 2
  Direction = (-1,0,0)
  FileGeomPattern = <path>
  FileHatchPattern = <path>
  Focus = 100
  FuseBeforeCut = false
  HardHidden = false
  HatchScale = 1
  IsoCount = 0
  IsoHidden = false
  IsoVisible = false
  LockPosition = true
  NameGeomPattern = Diamond
  Perspective = false
  Rotation = 0
  Scale = 0.5
  ScaleType = 2
  SeamHidden = false
  SeamVisible = true
  SectionDirection = 2
  SectionNormal = (-1,0,0)
  SectionOrigin = (2,-111.25,5)
  SectionSymbol = B
  SmoothHidden = false
  SmoothVisible = true
  Source = -> [Pad003]
  X = 77.4315
  XDirection = (0,-1,0)
  Y = 147.324
FEATURE [TechDraw::DrawViewDimension] Dimension024
  AngleOverride = false
  Arbitrary = false
  ArbitraryTolerances = false
  EqualTolerance = true
  ExtensionAngle = 0
  FormatSpec = %.2w
  FormatSpecOverTolerance = %+.2w
  FormatSpecUnderTolerance = %+.2w
  Inverted = false
  LineAngle = 0
  LockPosition = false
  MeasureType = 1
  OverTolerance = 0
  References2D = -> [SectionView001]
  Rotation = 0
  ScaleType = 0
  TheoreticalExact = false
  Type = 1
  UnderTolerance = 0
  X = -29.9379
  Y = -3.36393
FEATURE [TechDraw::DrawViewDimension] Dimension025
  AngleOverride = false
  Arbitrary = false
  ArbitraryTolerances = false
  EqualTolerance = true
  ExtensionAngle = 0
  FormatSpec = %.2w
  FormatSpecOverTolerance = %+.2w
  FormatSpecUnderTolerance = %+.2w
  Inverted = false
  LineAngle = 0
  LockPosition = false
  MeasureType = 1
  OverTolerance = 0
  References2D = -> [SectionView001]
  Rotation = 0
  ScaleType = 0
  TheoreticalExact = false
  Type = 1
  UnderTolerance = 0
  X = -5.88033
  Y = -3.23934
FEATURE [TechDraw::DrawViewDimension] Dimension026
  AngleOverride = false
  Arbitrary = false
  ArbitraryTolerances = false
  EqualTolerance = true
  ExtensionAngle = 0
  FormatSpec = %.2w
  FormatSpecOverTolerance = %+.2w
  FormatSpecUnderTolerance = %+.2w
  Inverted = false
  LineAngle = 0
  LockPosition = false
  MeasureType = 1
  OverTolerance = 0
  References2D = -> [SectionView001]
  Rotation = 0
  ScaleType = 0
  TheoreticalExact = false
  Type = 1
  UnderTolerance = 0
  X = 22.8117
  Y = -3.36393
FEATURE [TechDraw::DrawViewDimension] Dimension027
  AngleOverride = false
  Arbitrary = false
  ArbitraryTolerances = false
  EqualTolerance = true
  ExtensionAngle = 0
  FormatSpec = %.2w
  FormatSpecOverTolerance = %+.2w
  FormatSpecUnderTolerance = %+.2w
  Inverted = false
  LineAngle = 0
  LockPosition = false
  MeasureType = 1
  OverTolerance = 0
  References2D = -> [SectionView001]
  Rotation = 0
  ScaleType = 0
  TheoreticalExact = false
  Type = 2
  UnderTolerance = 0
  X = -57.5658
  Y = 4.47975
FEATURE [TechDraw::DrawViewAnnotation] Annotation003
  Font = osifont
  LineSpace = 80
  LockPosition = true
  MaxWidth = -1
  Rotation = 0
  ScaleType = 0
  Text = Sección B - B'
  TextSize = 5
  TextStyle = 0
  X = 45.0656
  Y = 154.564
FEATURE [TechDraw::DrawViewAnnotation] Annotation004
  Font = osifont
  LineSpace = 80
  LockPosition = true
  MaxWidth = -1
  Rotation = 0
  ScaleType = 0
  Text = '
  TextSize = 5
  TextStyle = 0
  X = 278.241
  Y = 86.8486
FEATURE [TechDraw::DrawPage] Page  label="Cubierta Superior"
  KeepUpdated = true
  NextBalloonIndex = 1
  ProjectionType = 0
  Template = -> Template
  Views = -> [ProjGroup,Dimension,Dimension001,Dimension002,Dimension003,Dimension004,Dimension005,Dimension006,Dimension007,Dimension008,Dimension009,Dimension010,Dimension011,Dimension012,Dimension013,Dimension014,Dimension015,SectionView,Dimension018,Annotation,Annotation001,Dimension020,Dimension021,Dimension022,Dimension023,Annotation002,SectionView001,Dimension024,Dimension025,Dimension026,Dimension027,+2 more]
note: 4 file-system paths scrubbed to <path> (originals preserved in the JSON sidecar)
